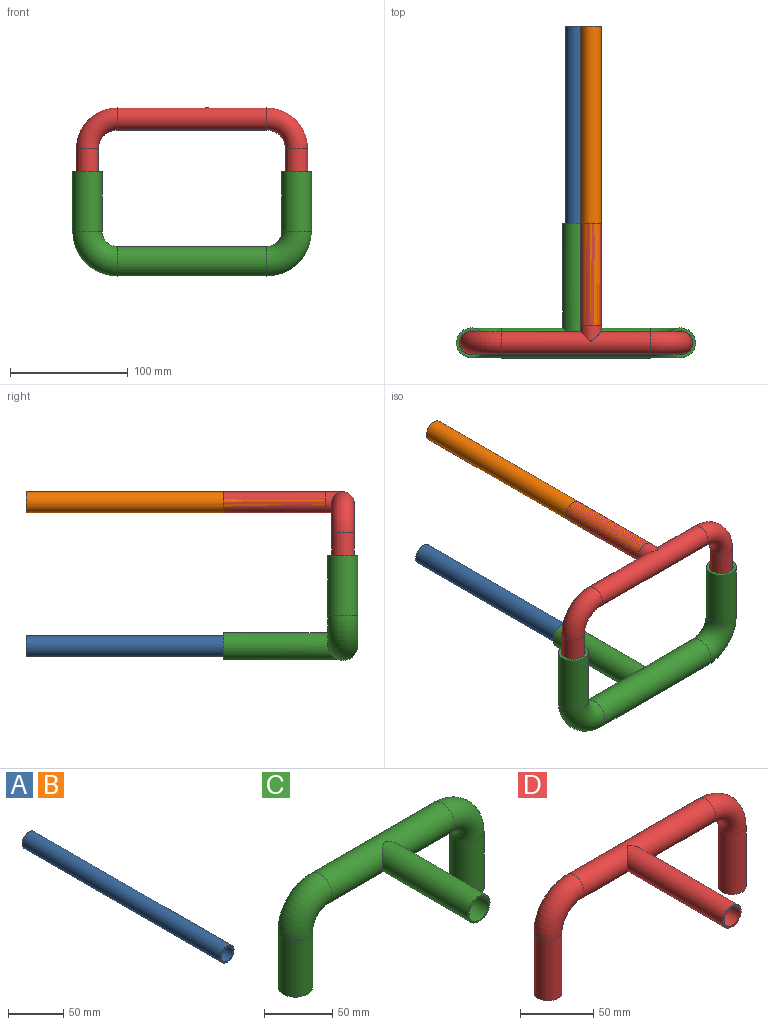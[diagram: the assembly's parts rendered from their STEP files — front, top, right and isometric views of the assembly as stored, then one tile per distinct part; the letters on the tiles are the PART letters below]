
ASSEMBLY  parts=4 mates=4
PART A: 4 faces, bbox 17.8x254x17.8 mm
  f0: cylinder r=7.62mm len=254mm, axis (0,1,0), area 12161mm2, adj f2,f3
  f1: cylinder r=8.89mm len=254mm, axis (0,1,0), area 14187.8mm2, adj f2,f3
  f2: plane 17.78x17.78mm, normal (0,-1,0), area 65.9mm2, adj f0,f1
  f3: plane 17.78x17.78mm, normal (0,1,0), area 65.9mm2, adj f0,f1
PART B: same geometry as A
PART C: 20 faces, bbox 209.5x114.3x92 mm
  f0: cylinder r=10.16mm len=127mm, axis (1,0,0), area 7971.5mm2, adj f3,f4,f16,f17,f18,f19
  f1: cylinder r=12.7mm len=127mm, axis (1,0,0), area 9656.2mm2, adj f9,f10,f13
  f2: cylinder r=10.16mm len=50.8mm, axis (0,0,1), area 3242.9mm2, adj f3,f6
  f3: torus R=25.4mm, axis (0,1,0), area 2547mm2, adj f0,f2
  f4: torus R=25.4mm, axis (0,1,0), area 2547mm2, adj f0,f5
  f5: cylinder r=10.16mm len=50.8mm, axis (0,0,-1), area 3242.9mm2, adj f4,f7
  f6: plane 25.4x25.4mm, normal (0,0,-1), area 182.4mm2, adj f2,f8
  f7: plane 25.4x25.4mm, normal (0,0,-1), area 182.4mm2, adj f5,f11
  f8: cylinder r=12.7mm len=50.8mm, axis (0,0,1), area 4053.7mm2, adj f6,f9
  f9: torus R=25.4mm, axis (0,1,0), area 3183.7mm2, adj f1,f8
  f10: torus R=25.4mm, axis (0,1,0), area 3183.7mm2, adj f1,f11
  f11: cylinder r=12.7mm len=50.8mm, axis (0,0,-1), area 4053.7mm2, adj f7,f10
  f12: plane 22.86x22.86mm, normal (0,-1,0), area 86.1mm2, adj f13,f14
  f13: cylinder r=11.43mm len=97.34mm, axis (0,1,0), area 6619.6mm2, adj f1,f12
  f14: cylinder r=10.16mm len=94.75mm, axis (0,1,0), area 5828.8mm2, adj f12,f15
  f15: cylinder r=12.7mm len=20.32mm, axis (1,0,0), area 360.8mm2, adj f14
  f16: cylinder r=10.16mm len=20.32mm, axis (0,1,0), area 412mm2, adj f0,f19
  f17: cylinder r=11.43mm len=20.32mm, axis (0,1,0), area 188.1mm2, adj f0,f19
  f18: cylinder r=11.43mm len=20.32mm, axis (0,1,0), area 188.1mm2, adj f0,f19
  f19: plane 22.86x20.32mm, normal (0,1,0), area 69.4mm2, adj f0,f16,f17,f18
PART D: 20 faces, bbox 202.6x111.1x88.6 mm
  f0: cylinder r=7.62mm len=127mm, axis (1,0,0), area 5984.1mm2, adj f3,f4,f16,f17,f18,f19
  f1: cylinder r=9.53mm len=127mm, axis (1,0,0), area 7302.5mm2, adj f9,f10,f13
  f2: cylinder r=7.62mm len=50.8mm, axis (0,0,1), area 2432.2mm2, adj f3,f6
  f3: torus R=25.4mm, axis (0,1,0), area 1910.2mm2, adj f0,f2
  f4: torus R=25.4mm, axis (0,1,0), area 1910.2mm2, adj f0,f5
  f5: cylinder r=7.62mm len=50.8mm, axis (0,0,-1), area 2432.2mm2, adj f4,f7
  f6: plane 19.05x19.05mm, normal (0,0,-1), area 102.6mm2, adj f2,f8
  f7: plane 19.05x19.05mm, normal (0,0,-1), area 102.6mm2, adj f5,f11
  f8: cylinder r=9.53mm len=50.8mm, axis (0,0,1), area 3040.2mm2, adj f6,f9
  f9: torus R=25.4mm, axis (0,1,0), area 2387.8mm2, adj f1,f8
  f10: torus R=25.4mm, axis (0,1,0), area 2387.8mm2, adj f1,f11
  f11: cylinder r=9.53mm len=50.8mm, axis (0,0,-1), area 3040.2mm2, adj f7,f10
  f12: plane 17.78x17.78mm, normal (0,-1,0), area 65.9mm2, adj f13,f14
  f13: cylinder r=8.89mm len=100.21mm, axis (0,1,0), area 5298.8mm2, adj f1,f12
  f14: cylinder r=7.62mm len=96.68mm, axis (0,1,0), area 4495.5mm2, adj f12,f15
  f15: cylinder r=9.53mm len=15.24mm, axis (1,0,0), area 203.3mm2, adj f14
  f16: cylinder r=7.62mm len=15.24mm, axis (0,1,0), area 231.4mm2, adj f0,f19
  f17: cylinder r=8.89mm len=15.24mm, axis (0,1,0), area 104.4mm2, adj f0,f19
  f18: cylinder r=8.89mm len=15.24mm, axis (0,1,0), area 104.3mm2, adj f0,f19
  f19: plane 17.78x15.24mm, normal (0,1,0), area 51.2mm2, adj f0,f16,f17,f18
PLACE A t=(-167.76,311.91,-250.44)mm
PLACE B t=(-154.97,311.91,-128.33)mm
PLACE C rot(axis=(1,0,0),180deg) t=(-256.66,169.97,-224.51)mm
PLACE D rot(axis=(0,0,1),180deg) t=(-78.86,169.97,-154.26)mm
MATE cylindrical B.f1 <-> D.f13  axis (0,1,0) through (-154.97,311.91,-128.33)mm
MATE cylindrical C.f13 <-> A.f1  axis (0,-1,0) through (-167.76,271.57,-250.44)mm
MATE planar A.f1 <-> B.f1  axis (0,1,0) through (-167.76,438.91,-250.44)mm
MATE cylindrical C.f2 <-> D.f11  axis (0,0,-1) through (-256.66,169.97,-199.11)mm
